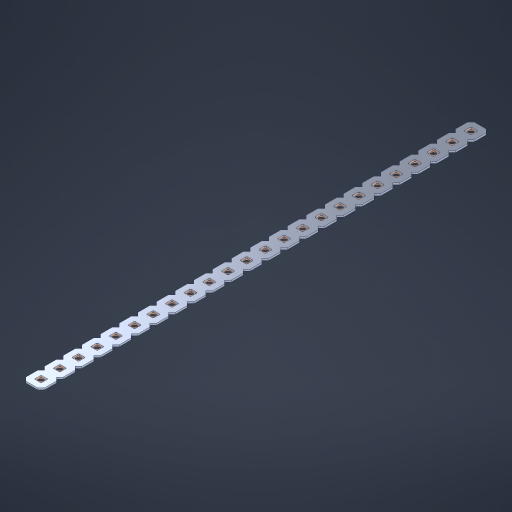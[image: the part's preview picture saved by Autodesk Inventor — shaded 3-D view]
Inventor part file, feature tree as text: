
AUTODESK INVENTOR PART (.ipt)
format: ipt  version: 2023 (Build 270158000, 158)  size: 567,808 bytes
history: native  units: in
note: dims shown in document units (in); Inventor stores cm internally (conversion verified against a paired STEP export)
features: other x25, extrude x23, sketch x2, pattern_linear x1
ambient origin geometry x8: Origin, YZ Plane, XZ Plane, XY Plane, X Axis, Y Axis, Z Axis, Center Point
bodies: Solid1 (feature_tree), Body (feature_tree)
feature tree (51):
  pattern_linear  "Rectangular Pattern1"  Spacing1=0.09in  [1 undecoded]
  sketch  "Sketch1"  dims[d1=0.5in]
  sketch  "Sketch2"  dims[d2=0.182in d3=0.09in d4=0.09in d5=0.09in d6=0.09in d7=0.09in d8=0.09in d9=0.09in d10=0.09in d11=0.02in d13=0.0in d14=0.172in d15=0.0625in d16=0.0in d19=0.5in d22=0.5in]
  other  "Srf1"
  other  "Srf126"
  other  "Srf127"
  other  "Srf128"
  other  "Srf129"
  other  "Srf130"
  other  "Srf131"
  other  "Srf250"
  other  "Srf251"
  other  "Srf252"
  other  "Srf253"
  other  "Srf254"
  other  "Srf255"
  other  "Srf256"
  other  "Srf257"
  other  "Srf258"
  other  "Srf259"
  other  "Srf260"
  other  "Srf261"
  other  "Srf262"
  other  "Srf263"
  other  "Srf264"
  other  "Srf265"
  other  "Srf266"
  other  "Circle"
  extrude  "ExtrusionSrf126"  Depth=0.09in
  extrude  "ExtrusionSrf127"  Depth=0.09in
  extrude  "ExtrusionSrf128"  Depth=0.09in
  extrude  "ExtrusionSrf129"  Depth=0.09in
  extrude  "ExtrusionSrf130"  Depth=0.09in
  extrude  "ExtrusionSrf131"  Depth=0.09in
  extrude  "ExtrusionSrf250"  Depth=0.09in
  extrude  "ExtrusionSrf251"  Depth=0.02in
  extrude  "ExtrusionSrf252"  TaperAngle=0.0deg  [1 undecoded]
  extrude  "ExtrusionSrf253"  Depth=0.5in
  extrude  "ExtrusionSrf254"  Depth=0.5in TaperAngle=0.0deg
  extrude  "ExtrusionSrf255"  Depth=0.5in
  extrude  "ExtrusionSrf256"  Depth=0.5in
  extrude  "ExtrusionSrf257"  [1 undecoded]
  extrude  "ExtrusionSrf258"  [1 undecoded]
  extrude  "ExtrusionSrf259"  [1 undecoded]
  extrude  "ExtrusionSrf260"  [1 undecoded]
  extrude  "ExtrusionSrf261"  [1 undecoded]
  extrude  "ExtrusionSrf262"  [1 undecoded]
  extrude  "ExtrusionSrf263"  [1 undecoded]
  extrude  "ExtrusionSrf264"  [1 undecoded]
  extrude  "ExtrusionSrf265"  [1 undecoded]
  extrude  "ExtrusionSrf266"  [1 undecoded]
note: 12 required parameter values undecoded (feature->parameter linkage not recoverable at this tier; creation-order binding heuristic only, values carry confidence <= 0.55)
